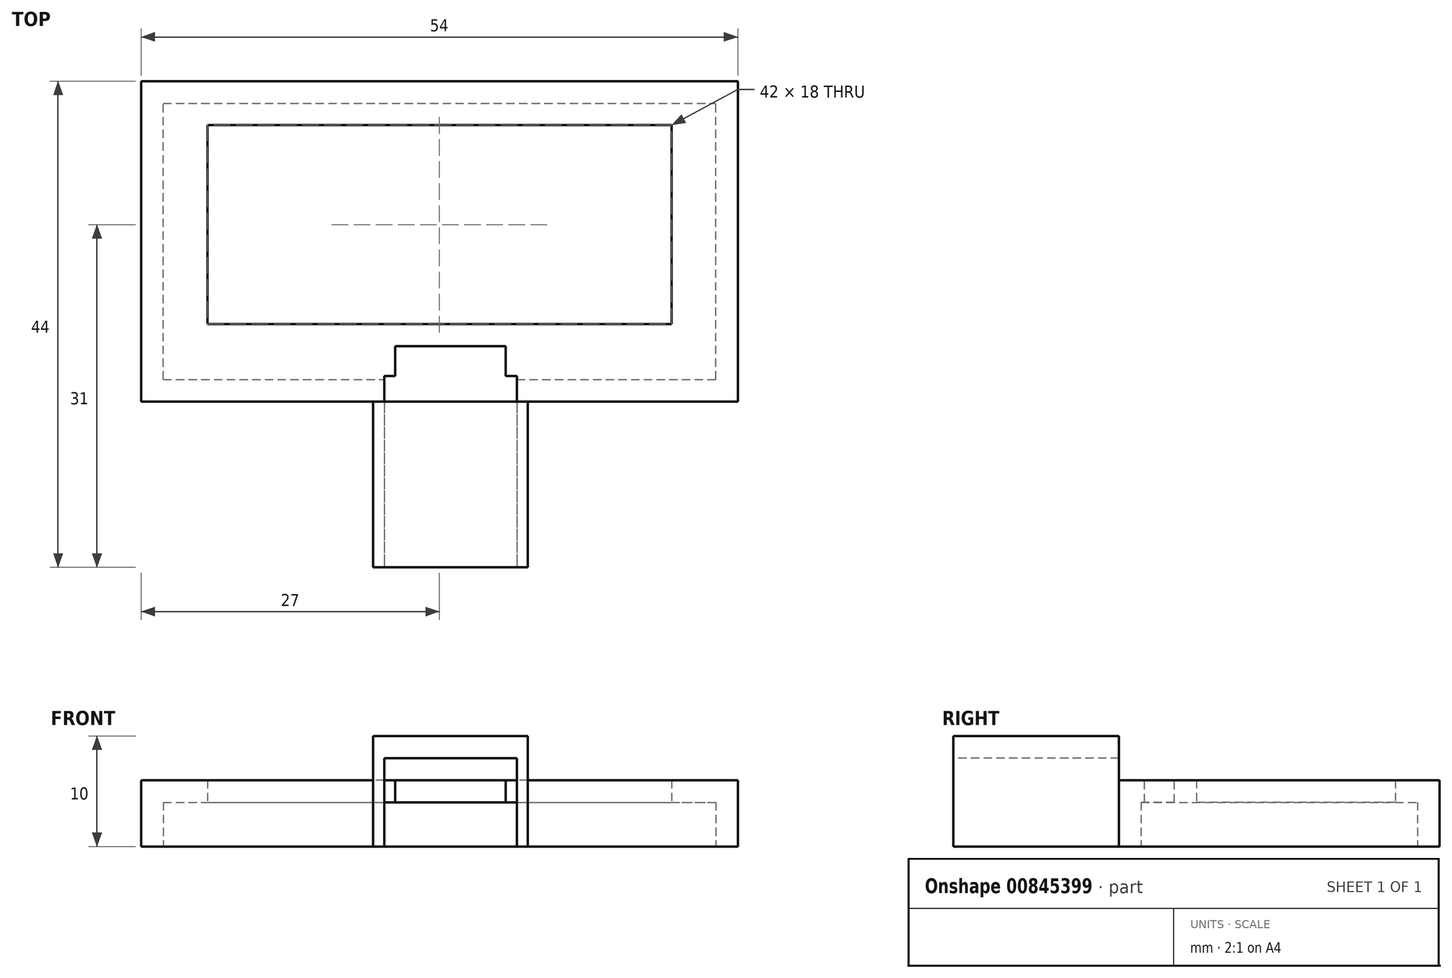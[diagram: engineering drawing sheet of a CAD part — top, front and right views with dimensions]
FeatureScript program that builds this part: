
annotation { "Feature Type Name" : "Feature", "Feature Type Description" : "" }
export const myFeature = defineFeature(function(context is Context, id is Id, definition is map)
    precondition{}
    {
        {
            var Q0;
            Q0=qCreatedBy(makeId("Top.planeOp"),FACE);
            var sketch = newSketch(context, id + "F0", { "sketchPlane" : qUnion([Q0])});
            skLineSegment(sketch, "E0.bottom", {"start": v(27, -14.5) * mm, "end": v(-27, -14.5) * mm});
            skLineSegment(sketch, "E0.top", {"start": v(27, 14.5) * mm, "end": v(-27, 14.5) * mm});
            skLineSegment(sketch, "E0.left", {"start": v(27, -14.5) * mm, "end": v(27, 14.5) * mm});
            skLineSegment(sketch, "E0.right", {"start": v(-27, -14.5) * mm, "end": v(-27, 14.5) * mm});
            skPoint(sketch, "E0.middle", {"position": v(0, 0) * mm});
            skSolve(sketch);
        }
        {
            var Q0;
            Q0=makeQuery(id+"F0.imprint","IMPRINT",FACE,{"disambiguationData":[TD([[makeQuery(id+"F0.imprint","IMPRINT",EDGE,{"derivedFrom":sQuery(id+"F0.wireOp",EDGE,"E0.bottom")}),-1.0]])]});
            var sketch = newSketch(context, id + "F1", { "sketchPlane" : qUnion([Q0])});
            skLineSegment(sketch, "E1.bottom", {"start": v(21, -7.5) * mm, "end": v(-21, -7.5) * mm});
            skLineSegment(sketch, "E1.top", {"start": v(21, 10.5) * mm, "end": v(-21, 10.5) * mm});
            skLineSegment(sketch, "E1.left", {"start": v(21, -7.5) * mm, "end": v(21, 10.5) * mm});
            skLineSegment(sketch, "E1.right", {"start": v(-21, -7.5) * mm, "end": v(-21, 10.5) * mm});
            skPoint(sketch, "E1.middle", {"position": v(0, 1.5) * mm});
            skSolve(sketch);
        }
        {
            var Q0;
            Q0 = qSketchRegion(id + "F0", true);
            extrude(context, id + "F2", {"entities" : qUnion([Q0]), "depth" : 6 * mm, "offsetDistance" : 25.4 * mm});
        }
        {
            var Q0;
            Q0 = qSketchRegion(id + "F1", true);
            extrude(context, id + "F3", {"entities" : qUnion([Q0]), "operationType" : NewBodyOperationType.REMOVE, "depth" : 25.4 * mm, "offsetDistance" : 25.4 * mm});
        }
        {
            var Q0;
            Q0=makeQuery(id+"F2.opExtrude","CAP_FACE",FACE,{"disambiguationData":[OSD([sQuery(id+"F0.wireOp",EDGE,"E0.bottom"),sQuery(id+"F0.wireOp",EDGE,"E0.top"),sQuery(id+"F0.wireOp",EDGE,"E0.left"),sQuery(id+"F0.wireOp",EDGE,"E0.right")])],"isStart":true});
            var sketch = newSketch(context, id + "F4", { "sketchPlane" : qUnion([Q0])});
            skLineSegment(sketch, "E2.bottom", {"start": v(-25, 12.5) * mm, "end": v(25, 12.5) * mm});
            skLineSegment(sketch, "E2.top", {"start": v(-25, -12.5) * mm, "end": v(25, -12.5) * mm});
            skLineSegment(sketch, "E2.left", {"start": v(-25, 12.5) * mm, "end": v(-25, -12.5) * mm});
            skLineSegment(sketch, "E2.right", {"start": v(25, 12.5) * mm, "end": v(25, -12.5) * mm});
            skPoint(sketch, "E2.middle", {"position": v(0, 0) * mm});
            skSolve(sketch);
        }
        {
            var Q0;
            Q0 = qSketchRegion(id + "F4", true);
            extrude(context, id + "F5", {"entities" : qUnion([Q0]), "operationType" : NewBodyOperationType.REMOVE, "oppositeDirection" : true, "depth" : 4 * mm, "offsetDistance" : 25.4 * mm});
        }
        {
            var Q0;
            Q0=makeQuery(id+"F2.opExtrude","SWEPT_FACE",FACE,{"disambiguationData":[OSD([sQuery(id+"F0.wireOp",EDGE,"E0.bottom")])]});
            var sketch = newSketch(context, id + "F6", { "sketchPlane" : qUnion([Q0])});
            skLineSegment(sketch, "E3.bottom", {"start": v(6, 0) * mm, "end": v(-4, 0) * mm});
            skLineSegment(sketch, "E3.top", {"start": v(6, 6) * mm, "end": v(-4, 6) * mm});
            skLineSegment(sketch, "E3.left", {"start": v(6, 0) * mm, "end": v(6, 6) * mm});
            skLineSegment(sketch, "E3.right", {"start": v(-4, 0) * mm, "end": v(-4, 6) * mm});
            skSolve(sketch);
        }
        {
            var Q0;
            Q0=makeQuery(id+"F6.imprint","IMPRINT",FACE,{"disambiguationData":[TD([[makeQuery(id+"F6.imprint","IMPRINT",EDGE,{"derivedFrom":sQuery(id+"F6.wireOp",EDGE,"E3.bottom")}),-1.0]])]});
            extrude(context, id + "F7", {"entities" : qUnion([Q0]), "operationType" : NewBodyOperationType.REMOVE, "oppositeDirection" : true, "depth" : 5 * mm, "offsetDistance" : 25.4 * mm});
        }
        {
            var Q0;
            {var subQ1=sQuery(id+"F0.wireOp",EDGE,"E0.left");var subQ3=sQuery(id+"F0.wireOp",EDGE,"E0.bottom");Q0=makeQuery(id+"F7.boolean.opBoolean","SPLIT",FACE,{"disambiguationData":[TD([makeQuery(id+"F2.opExtrude","SWEPT_FACE",FACE,{"disambiguationData":[OSD([subQ1])]})])],"derivedFrom":makeQuery(id+"F2.opExtrude","SWEPT_FACE",FACE,{"disambiguationData":[OSD([subQ3])]})});}
            var sketch = newSketch(context, id + "F8", { "sketchPlane" : qUnion([Q0])});
            skLineSegment(sketch, "E4.bottom", {"start": v(-6, 0) * mm, "end": v(8, 0) * mm});
            skLineSegment(sketch, "E4.top", {"start": v(-6, 10) * mm, "end": v(8, 10) * mm});
            skLineSegment(sketch, "E4.left", {"start": v(-6, 0) * mm, "end": v(-6, 10) * mm});
            skLineSegment(sketch, "E4.right", {"start": v(8, 0) * mm, "end": v(8, 10) * mm});
            skSolve(sketch);
        }
        {
            var Q0;
            Q0 = qSketchRegion(id + "F8", true);
            extrude(context, id + "F9", {"entities" : qUnion([Q0]), "operationType" : NewBodyOperationType.ADD, "depth" : 15 * mm, "offsetDistance" : 25.4 * mm});
        }
        {
            var Q0;
            Q0=makeQuery(id+"F9.boolean.opBoolean","MERGE",FACE,{"derivedFrom":[makeQuery(id+"F2.opExtrude","CAP_FACE",FACE,{"disambiguationData":[OSD([sQuery(id+"F0.wireOp",EDGE,"E0.bottom"),sQuery(id+"F0.wireOp",EDGE,"E0.top"),sQuery(id+"F0.wireOp",EDGE,"E0.left"),sQuery(id+"F0.wireOp",EDGE,"E0.right")])],"isStart":true}),makeQuery(id+"F9.opExtrude","SWEPT_FACE",FACE,{"disambiguationData":[OSD([sQuery(id+"F8.wireOp",EDGE,"E4.bottom")])]})]});
            var sketch = newSketch(context, id + "F10", { "sketchPlane" : qUnion([Q0])});
            skLineSegment(sketch, "E5.bottom", {"start": v(-5, 12.18) * mm, "end": v(7, 12.18) * mm});
            skLineSegment(sketch, "E5.top", {"start": v(-5, 30.9) * mm, "end": v(7, 30.9) * mm});
            skLineSegment(sketch, "E5.left", {"start": v(-5, 12.18) * mm, "end": v(-5, 30.9) * mm});
            skLineSegment(sketch, "E5.right", {"start": v(7, 12.18) * mm, "end": v(7, 30.9) * mm});
            skSolve(sketch);
        }
        {
            var Q0;
            Q0 = qSketchRegion(id + "F10", true);
            extrude(context, id + "F11", {"entities" : qUnion([Q0]), "operationType" : NewBodyOperationType.REMOVE, "oppositeDirection" : true, "depth" : 8 * mm, "offsetDistance" : 25.4 * mm});
        }
    });
